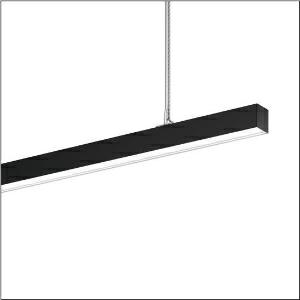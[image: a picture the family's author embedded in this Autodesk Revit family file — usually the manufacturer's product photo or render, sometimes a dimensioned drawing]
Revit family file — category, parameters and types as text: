
# Revit family: silica_r__21_51mx30tct9b_d278
name_source: partatom
category: Lighting Fixtures
units: mm (PartAtom-declared; Revit-internal decimal feet)

## family parameters
Cut with Voids When Loaded = No
Host = Face
Light Source = No
Part Type = Normal
Room Calculation Point = No
Round Connector Dimension = Use Diameter
Shared = No

## types (1)
- --- (1 x LED, 10300 lm, 84.4 W, 6500K)
    Apparent Load = 84 VA
    CIE Flux Codes = 47 79 96 58 100
    Color Rendering = 80
    Color Temperature = 6500K
    Default Elevation = 1800 mm
    Description = Silica® 21, office luminaire, primary optical cover: cover, of PMMA, opal, light emission: direct/indirect distribution, primary light characteristic: symmetric, installation type: suspended mounting, LED, rated luminous flux: 10.300lm, luminous efficacy: 116lm/W, light colour: 8tw, colour temperature: 2700..6500K, control gear: ECG DALI, with terminal, 3+2-pole, max. 2.5mm², mains connection: 220..240V, AC, 50/60Hz, rated input power: 88.7W, luminaire housing, of aluminium, jet black (RAL 9005), length: 3.004mm, width: 53mm, height: 53mm, protection rating (complete): IP20, insulation class (complete): insulation class I (protective earthing), certification: CE, permissible operating ambient temperature: 0..+35°C, standard: EN 50419, packaging unit: 1 piece
    Height = 53 mm
    Lamp = 1 x LED
    Lamp Light Flux = 10300 lm
    Lamp Power = 84.4 W
    Lamp count = 1
    Length = 3004 mm
    Luminous efficacy = 122 lm/W
    Manufacturer = Siteco
    ModVariant = No
    Model = 51MX30TCT9B
    Mounting Place = Ceiling
    Mounting Type = Pendant
    Number of Poles = 1
    OnlyDefault = Yes
    Power Factor = 1
    Product Name = Silica® 21
    Product group = office luminaire | ceiling pendant
    ProductGroupID = 902
    Protection Class = Protection class I
    Protection Degree = IP 20
    RLX_Detail_Level = 1
    RLX_Emergency_Light_Flux = 0 lm
    RLX_Emergency_Type = 0
    RLX_Emergency_Type_DB = No
    RlxData = <blob elided: 22765 chars, md5=320edfb4>
    Socket = socket
    Standby Power = 0 W
    System Light Flux = 10300 lm
    System Power = 84 W
    Type Comments = individual setting
    Type Image = l_1313646.jpg
    URL = http://relux.com
    VarID = @adj_088995
    Voltage = 0 V
    Weight = 0.00 kg
    Width = 53 mm

## geometry (parser evidence)
native form markers: Blend x4, Sweep x12
no freeform markers — native parametric forms only
